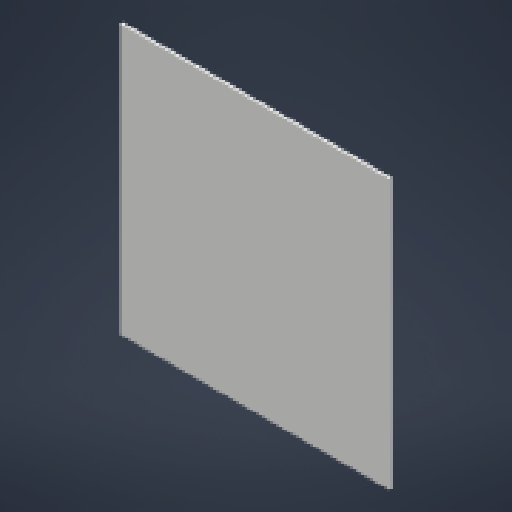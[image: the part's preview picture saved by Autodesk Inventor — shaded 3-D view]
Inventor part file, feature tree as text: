
AUTODESK INVENTOR PART (.ipt)
format: ipt  version: 2024 (Build 280153000, 153)  size: 116,736 bytes
history: native  units: mm
features: other x2, extrude x1, sketch x1
ambient origin geometry x8: Origin, YZ Plane, XZ Plane, XY Plane, X Axis, Y Axis, Z Axis, Center Point
bodies: Body1 (feature_tree)
feature tree (4):
  other  "솔리드1"
  extrude  "돌출1"  Depth=500.0mm
  sketch  "스케치1"
  other  "Finish1"
